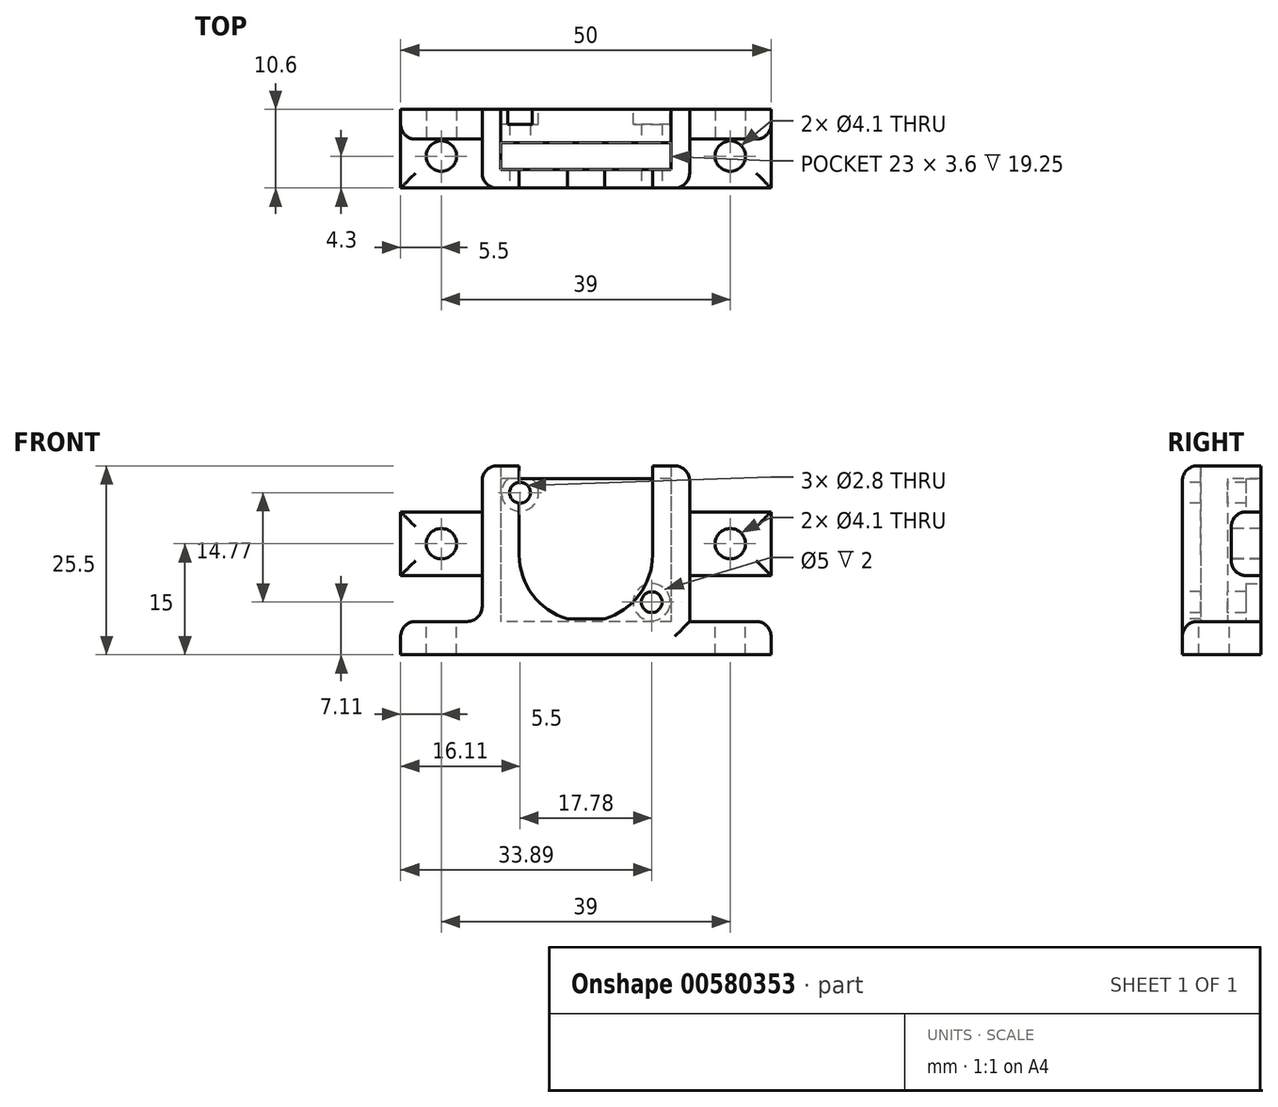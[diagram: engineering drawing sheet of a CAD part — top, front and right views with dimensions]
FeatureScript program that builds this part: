
annotation { "Feature Type Name" : "Feature", "Feature Type Description" : "" }
export const myFeature = defineFeature(function(context is Context, id is Id, definition is map)
    precondition{}
    {
        {
            var Q0;
            Q0=qCreatedBy(makeId("Top.planeOp"),FACE);
            var sketch = newSketch(context, id + "F0", { "sketchPlane" : qUnion([Q0])});
            skLineSegment(sketch, "E0.bottom", {"start": v(11.5, -1.8) * mm, "end": v(-11.5, -1.8) * mm});
            skLineSegment(sketch, "E0.top", {"start": v(11.5, 1.8) * mm, "end": v(-11.5, 1.8) * mm});
            skLineSegment(sketch, "E0.left", {"start": v(11.5, -1.8) * mm, "end": v(11.5, 1.8) * mm});
            skLineSegment(sketch, "E0.right", {"start": v(-11.5, -1.8) * mm, "end": v(-11.5, 1.8) * mm});
            skPoint(sketch, "E0.middle", {"position": v(0, 0) * mm});
            skLineSegment(sketch, "E1.bottom", {"start": v(14, -4.3) * mm, "end": v(-14, -4.3) * mm});
            skLineSegment(sketch, "E1.top", {"start": v(14, 4.3) * mm, "end": v(-14, 4.3) * mm});
            skLineSegment(sketch, "E1.left", {"start": v(14, -4.3) * mm, "end": v(14, 4.3) * mm});
            skLineSegment(sketch, "E1.right", {"start": v(-14, -4.3) * mm, "end": v(-14, 4.3) * mm});
            skSolve(sketch);
        }
        {
            var Q0;
            Q0 = qSketchRegion(id + "F0", true);
            extrude(context, id + "F1", {"entities" : qUnion([Q0]), "depth" : 21 * mm, "offsetDistance" : 25 * mm});
        }
        {
            var Q0;
            Q0=makeQuery(id+"F1.opExtrude","SWEPT_FACE",FACE,{"disambiguationData":[OSD([sQuery(id+"F0.wireOp",EDGE,"E1.bottom")])]});
            var sketch = newSketch(context, id + "F2", { "sketchPlane" : qUnion([Q0])});
            skPoint(sketch, "E2.start.orphan", {"position": v(-7.75, 9) * mm});
            skPoint(sketch, "E3.start.orphan", {"position": v(9.75, 9) * mm});
            skPoint(sketch, "E4.center.orphan", {"position": v(1, 9) * mm});
            skArc(sketch, "E5", {"start": v(-9, 9) * mm, "mid": v(-7.2, 3.6) * mm, "end": v(-2.5, 0.36) * mm});
            skLineSegment(sketch, "E6", {"start": v(9, 9) * mm, "end": v(9, 21) * mm});
            skLineSegment(sketch, "E7", {"start": v(-9, 9) * mm, "end": v(-9, 21) * mm});
            skPoint(sketch, "E8.orphan", {"position": v(-14, 9) * mm});
            skPoint(sketch, "E9.orphan", {"position": v(14, 9) * mm});
            skLineSegment(sketch, "E10", {"start": v(2.5, 0.36) * mm, "end": v(-2.5, 0.36) * mm});
            skArc(sketch, "E11.trimOffspring", {"start": v(2.5, 0.36) * mm, "mid": v(7.2, 3.6) * mm, "end": v(9, 9) * mm});
            skSolve(sketch);
        }
        {
            var Q0;
            Q0=makeQuery(id+"F2.imprint","IMPRINT",FACE,{"disambiguationData":[TD([[makeQuery(id+"F2.imprint","IMPRINT",EDGE,{"derivedFrom":sQuery(id+"F2.wireOp",EDGE,"E5")}),1.0]])]});
            extrude(context, id + "F3", {"entities" : qUnion([Q0]), "operationType" : NewBodyOperationType.REMOVE, "oppositeDirection" : true, "depth" : 2.5 * mm, "offsetDistance" : 25 * mm});
        }
        {
            var Q0;
            Q0=makeQuery(id+"F1.opExtrude","CAP_FACE",FACE,{"disambiguationData":[OSD([sQuery(id+"F0.wireOp",EDGE,"E0.bottom"),sQuery(id+"F0.wireOp",EDGE,"E0.top"),sQuery(id+"F0.wireOp",EDGE,"E0.left"),sQuery(id+"F0.wireOp",EDGE,"E0.right"),sQuery(id+"F0.wireOp",EDGE,"E1.bottom"),sQuery(id+"F0.wireOp",EDGE,"E1.top"),sQuery(id+"F0.wireOp",EDGE,"E1.left"),sQuery(id+"F0.wireOp",EDGE,"E1.right")])],"isStart":true});
            var sketch = newSketch(context, id + "F4", { "sketchPlane" : qUnion([Q0])});
            skLineSegment(sketch, "E12.bottom", {"start": v(-25, -4.3) * mm, "end": v(25, -4.3) * mm});
            skLineSegment(sketch, "E12.top", {"start": v(-25, 4.3) * mm, "end": v(25, 4.3) * mm});
            skLineSegment(sketch, "E12.left", {"start": v(-25, -4.3) * mm, "end": v(-25, 4.3) * mm});
            skLineSegment(sketch, "E12.right", {"start": v(25, -4.3) * mm, "end": v(25, 4.3) * mm});
            skPoint(sketch, "E12.middle", {"position": v(0, 0) * mm});
            skSolve(sketch);
        }
        {
            var Q0;
            Q0 = qSketchRegion(id + "F4", true);
            extrude(context, id + "F5", {"entities" : qUnion([Q0]), "operationType" : NewBodyOperationType.ADD, "depth" : 2.5 * mm, "offsetDistance" : 25 * mm});
        }
        {
            var Q0;
            {var subQ0=sQuery(id+"F4.wireOp",EDGE,"E12.top");var subQ1=sQuery(id+"F4.wireOp",EDGE,"E12.bottom");var subQ2=sQuery(id+"F4.wireOp",EDGE,"E12.left");Q0=makeQuery(id+"F5.boolean.opBoolean","SPLIT",FACE,{"disambiguationData":[TD([makeQuery(id+"F1.opExtrude","SWEPT_FACE",FACE,{"disambiguationData":[OSD([sQuery(id+"F0.wireOp",EDGE,"E1.right")])]})])],"derivedFrom":makeQuery(id+"F5.opExtrude","CAP_FACE",FACE,{"disambiguationData":[OSD([subQ1,subQ0,subQ2,sQuery(id+"F4.wireOp",EDGE,"E12.right")])],"isStart":true})});}
            var sketch = newSketch(context, id + "F6", { "sketchPlane" : qUnion([Q0])});
            skCircle(sketch, "E13", {"center": v(-19.5, 0) * mm, "radius": 2.05 * mm});
            skPoint(sketch, "E13.centerSnap0", {"position": v(-19.5, -2.3) * mm});
            skLineSegment(sketch, "E14", {"start": v(-19.5, -4.3) * mm, "end": v(-19.5, 4.3) * mm});
            skSolve(sketch);
        }
        {
            var Q0;
            Q0 = qSketchRegion(id + "F6", true);
            extrude(context, id + "F7", {"entities" : qUnion([Q0]), "operationType" : NewBodyOperationType.REMOVE, "oppositeDirection" : true, "depth" : 25 * mm, "offsetDistance" : 25 * mm});
        }
        {
            var Q0;
            {var subQ0=sQuery(id+"F4.wireOp",EDGE,"E12.bottom");var subQ1=sQuery(id+"F4.wireOp",EDGE,"E12.top");var subQ2=sQuery(id+"F4.wireOp",EDGE,"E12.right");Q0=makeQuery(id+"F5.boolean.opBoolean","SPLIT",FACE,{"disambiguationData":[TD([makeQuery(id+"F1.opExtrude","SWEPT_FACE",FACE,{"disambiguationData":[OSD([sQuery(id+"F0.wireOp",EDGE,"E1.left")])]})])],"derivedFrom":makeQuery(id+"F5.opExtrude","CAP_FACE",FACE,{"disambiguationData":[OSD([subQ0,subQ1,sQuery(id+"F4.wireOp",EDGE,"E12.left"),subQ2])],"isStart":true})});}
            var sketch = newSketch(context, id + "F8", { "sketchPlane" : qUnion([Q0])});
            skCircle(sketch, "E15", {"center": v(19.5, 0) * mm, "radius": 2.05 * mm});
            skPoint(sketch, "E15.centerSnap0", {"position": v(19.5, -2.05) * mm});
            skLineSegment(sketch, "E16", {"start": v(19.5, -4.3) * mm, "end": v(19.5, 4.3) * mm});
            skSolve(sketch);
        }
        {
            var Q0;
            Q0 = qSketchRegion(id + "F8", true);
            extrude(context, id + "F9", {"entities" : qUnion([Q0]), "operationType" : NewBodyOperationType.REMOVE, "oppositeDirection" : true, "depth" : 25 * mm, "offsetDistance" : 25 * mm});
        }
        {
            var Q0;
            Q0=makeQuery(id+"F1.opExtrude","CAP_FACE",FACE,{"disambiguationData":[OSD([sQuery(id+"F0.wireOp",EDGE,"E0.bottom"),sQuery(id+"F0.wireOp",EDGE,"E0.top"),sQuery(id+"F0.wireOp",EDGE,"E0.left"),sQuery(id+"F0.wireOp",EDGE,"E0.right"),sQuery(id+"F0.wireOp",EDGE,"E1.bottom"),sQuery(id+"F0.wireOp",EDGE,"E1.top"),sQuery(id+"F0.wireOp",EDGE,"E1.left"),sQuery(id+"F0.wireOp",EDGE,"E1.right")])],"isStart":false});
            var sketch = newSketch(context, id + "F10", { "sketchPlane" : qUnion([Q0])});
            skLineSegment(sketch, "E17.bottom", {"start": v(-11.5, -1.7) * mm, "end": v(11.5, -1.7) * mm});
            skLineSegment(sketch, "E17.top", {"start": v(-11.5, 1.7) * mm, "end": v(11.5, 1.7) * mm});
            skLineSegment(sketch, "E17.left", {"start": v(-11.5, -1.7) * mm, "end": v(-11.5, 1.7) * mm});
            skLineSegment(sketch, "E17.right", {"start": v(11.5, -1.7) * mm, "end": v(11.5, 1.7) * mm});
            skSolve(sketch);
        }
        {
            var Q0;
            Q0 = qSketchRegion(id + "F10", true);
            extrude(context, id + "F11", {"entities" : qUnion([Q0]), "operationType" : NewBodyOperationType.REMOVE, "oppositeDirection" : true, "depth" : 21 * mm, "offsetDistance" : 25 * mm});
        }
        {
            var Q0;
            Q0=makeQuery(id+"F1.opExtrude","SWEPT_FACE",FACE,{"disambiguationData":[OSD([sQuery(id+"F0.wireOp",EDGE,"E0.top")])]});
            var sketch = newSketch(context, id + "F12", { "sketchPlane" : qUnion([Q0])});
            skLineSegment(sketch, "E18.bottom", {"start": v(11.5, 17.25) * mm, "end": v(-11.5, 17.25) * mm});
            skLineSegment(sketch, "E18.top", {"start": v(11.5, 24.75) * mm, "end": v(-11.5, 24.75) * mm});
            skLineSegment(sketch, "E18.left", {"start": v(11.5, 17.25) * mm, "end": v(11.5, 24.75) * mm});
            skLineSegment(sketch, "E18.right", {"start": v(-11.5, 17.25) * mm, "end": v(-11.5, 24.75) * mm});
            skPoint(sketch, "E18.middle", {"position": v(0, 21) * mm});
            skSolve(sketch);
        }
        {
            var Q0;
            {var subQ0=sQuery(id+"F12.wireOp",EDGE,"E18.bottom");Q0=makeQuery(id+"F12.imprint","IMPRINT",FACE,{"disambiguationData":[TD([[makeQuery(id+"F12.imprint","IMPRINT",EDGE,{"derivedFrom":subQ0}),-1.0]])]});}
            extrude(context, id + "F13", {"entities" : qUnion([Q0]), "operationType" : NewBodyOperationType.REMOVE, "oppositeDirection" : true, "depth" : 25 * mm, "offsetDistance" : 25 * mm});
        }
        {
            var Q0;
            Q0=makeQuery(id+"F1.opExtrude","SWEPT_FACE",FACE,{"disambiguationData":[OSD([sQuery(id+"F0.wireOp",EDGE,"E1.left")])]});
            var sketch = newSketch(context, id + "F14", { "sketchPlane" : qUnion([Q0])});
            skLineSegment(sketch, "E19", {"start": v(4.3, 10.5) * mm, "end": v(4.3, 14.8) * mm});
            skLineSegment(sketch, "E20", {"start": v(4.3, 14.8) * mm, "end": v(4.3, 6.2) * mm});
            skLineSegment(sketch, "E21", {"start": v(4.3, 6.2) * mm, "end": v(2.3, 6.2) * mm});
            skLineSegment(sketch, "E22", {"start": v(2.3, 6.2) * mm, "end": v(2.3, 14.8) * mm});
            skLineSegment(sketch, "E23", {"start": v(2.3, 14.8) * mm, "end": v(4.3, 14.8) * mm});
            skSolve(sketch);
        }
        {
            var Q0;
            Q0 = qSketchRegion(id + "F14", true);
            extrude(context, id + "F15", {"entities" : qUnion([Q0]), "operationType" : NewBodyOperationType.ADD, "depth" : 11 * mm, "offsetDistance" : 25 * mm});
        }
        {
            var Q0;
            Q0=makeQuery(id+"F1.opExtrude","SWEPT_FACE",FACE,{"disambiguationData":[OSD([sQuery(id+"F0.wireOp",EDGE,"E1.right")])]});
            var sketch = newSketch(context, id + "F16", { "sketchPlane" : qUnion([Q0])});
            skLineSegment(sketch, "E24.bottom", {"start": v(-2.3, 14.8) * mm, "end": v(-6.3, 14.8) * mm});
            skLineSegment(sketch, "E24.top", {"start": v(-2.3, 6.2) * mm, "end": v(-6.3, 6.2) * mm});
            skLineSegment(sketch, "E24.left", {"start": v(-2.3, 14.8) * mm, "end": v(-2.3, 6.2) * mm});
            skPoint(sketch, "E24.middle", {"position": v(-4.3, 10.5) * mm});
            skLineSegment(sketch, "E25", {"start": v(-4.3, 6.2) * mm, "end": v(-4.3, 14.8) * mm});
            skSolve(sketch);
        }
        {
            var Q0;
            Q0 = qSketchRegion(id + "F16", true);
            extrude(context, id + "F17", {"entities" : qUnion([Q0]), "operationType" : NewBodyOperationType.ADD, "depth" : 11 * mm, "offsetDistance" : 25 * mm});
        }
        {
            var Q0;
            Q0=makeQuery(id+"F17.opExtrude","SWEPT_FACE",FACE,{"disambiguationData":[OSD([sQuery(id+"F16.wireOp",EDGE,"E24.left")])]});
            var sketch = newSketch(context, id + "F18", { "sketchPlane" : qUnion([Q0])});
            skLineSegment(sketch, "E26", {"start": v(-19.5, 6.2) * mm, "end": v(-19.5, 14.8) * mm});
            skCircle(sketch, "E27", {"center": v(-19.5, 10.5) * mm, "radius": 2.05 * mm});
            skSolve(sketch);
        }
        {
            var Q0;
            Q0=makeQuery(id+"F15.opExtrude","SWEPT_FACE",FACE,{"disambiguationData":[OSD([sQuery(id+"F14.wireOp",EDGE,"E22")])]});
            var sketch = newSketch(context, id + "F19", { "sketchPlane" : qUnion([Q0])});
            skLineSegment(sketch, "E28", {"start": v(19.5, 6.2) * mm, "end": v(19.5, 14.8) * mm});
            skCircle(sketch, "E29", {"center": v(19.5, 10.5) * mm, "radius": 2.05 * mm});
            skSolve(sketch);
        }
        {
            var Q0;
            {var subQ0=sQuery(id+"F18.wireOp",EDGE,"E27");var subQ1=sQuery(id+"F18.wireOp",EDGE,"E26");var subQ2=makeQuery(id+"F18.imprint","INTERSECT",VERTEX,{"disambiguationData":[OD(0.0)],"derivedFrom":[subQ1,subQ0]});Q0=makeQuery(id+"F18.imprint","IMPRINT",FACE,{"disambiguationData":[TD([[makeQuery(id+"F18.imprint","IMPRINT",EDGE,{"disambiguationData":[TD([[subQ2,-1.0]])],"derivedFrom":subQ1}),-1.0]])]});}
            var Q1;
            {var subQ0=sQuery(id+"F18.wireOp",EDGE,"E27");var subQ1=sQuery(id+"F18.wireOp",EDGE,"E26");var subQ2=makeQuery(id+"F18.imprint","INTERSECT",VERTEX,{"disambiguationData":[OD(0.0)],"derivedFrom":[subQ1,subQ0]});Q1=makeQuery(id+"F18.imprint","IMPRINT",FACE,{"disambiguationData":[TD([[makeQuery(id+"F18.imprint","IMPRINT",EDGE,{"disambiguationData":[TD([[subQ2,-1.0]])],"derivedFrom":subQ1}),1.0]])]});}
            var Q2;
            {var subQ0=sQuery(id+"F19.wireOp",EDGE,"E29");var subQ1=sQuery(id+"F19.wireOp",EDGE,"E28");var subQ2=makeQuery(id+"F19.imprint","INTERSECT",VERTEX,{"disambiguationData":[OD(0.0)],"derivedFrom":[subQ1,subQ0]});Q2=makeQuery(id+"F19.imprint","IMPRINT",FACE,{"disambiguationData":[TD([[makeQuery(id+"F19.imprint","IMPRINT",EDGE,{"disambiguationData":[TD([[subQ2,-1.0]])],"derivedFrom":subQ1}),1.0]])]});}
            var Q3;
            {var subQ0=sQuery(id+"F19.wireOp",EDGE,"E29");var subQ1=sQuery(id+"F19.wireOp",EDGE,"E28");var subQ2=makeQuery(id+"F19.imprint","INTERSECT",VERTEX,{"disambiguationData":[OD(0.0)],"derivedFrom":[subQ1,subQ0]});Q3=makeQuery(id+"F19.imprint","IMPRINT",FACE,{"disambiguationData":[TD([[makeQuery(id+"F19.imprint","IMPRINT",EDGE,{"disambiguationData":[TD([[subQ2,-1.0]])],"derivedFrom":subQ1}),-1.0]])]});}
            extrude(context, id + "F20", {"entities" : qUnion([Q0, Q1, Q2, Q3]), "operationType" : NewBodyOperationType.REMOVE, "oppositeDirection" : true, "depth" : 25 * mm, "offsetDistance" : 25 * mm});
        }
        {
            var Q0;
            Q0=makeQuery(id+"F5.opExtrude","CAP_EDGE",EDGE,{"disambiguationData":[OSD([sQuery(id+"F4.wireOp",EDGE,"E12.left")])],"isStart":true});
            var Q1;
            {var subQ0=sQuery(id+"F4.wireOp",EDGE,"E12.top");Q1=makeQuery(id+"F5.boolean.opBoolean","SPLIT",EDGE,{"disambiguationData":[TD([makeQuery(id+"F1.opExtrude","SWEPT_FACE",FACE,{"disambiguationData":[OSD([sQuery(id+"F0.wireOp",EDGE,"E1.right")])]})])],"derivedFrom":makeQuery(id+"F5.opExtrude","CAP_EDGE",EDGE,{"disambiguationData":[OSD([subQ0])],"isStart":true})});}
            var Q2;
            Q2=makeQuery(id+"F1.opExtrude","SWEPT_EDGE",EDGE,{"disambiguationData":[OSD([sQuery(id+"F0.wireOp",EDGE,"E1.bottom"),sQuery(id+"F0.wireOp",EDGE,"E1.right")])]});
            var Q3;
            Q3=makeQuery(id+"F1.opExtrude","CAP_EDGE",EDGE,{"disambiguationData":[OSD([sQuery(id+"F0.wireOp",EDGE,"E1.right")])],"isStart":true});
            var Q4;
            Q4=makeQuery(id+"F1.opExtrude","CAP_EDGE",EDGE,{"disambiguationData":[OSD([sQuery(id+"F0.wireOp",EDGE,"E1.right")])],"isStart":false});
            var Q5;
            {var subQ0=sQuery(id+"F0.wireOp",EDGE,"E1.right");var subQ1=sQuery(id+"F0.wireOp",EDGE,"E1.bottom");Q5=makeQuery(id+"F3.boolean.opBoolean","SPLIT",EDGE,{"disambiguationData":[TD([makeQuery(id+"F1.opExtrude","SWEPT_FACE",FACE,{"disambiguationData":[OSD([subQ0])]})])],"derivedFrom":makeQuery(id+"F1.opExtrude","CAP_EDGE",EDGE,{"disambiguationData":[OSD([subQ1])],"isStart":false})});}
            var Q6;
            {var subQ0=sQuery(id+"F4.wireOp",EDGE,"E12.top");Q6=makeQuery(id+"F5.boolean.opBoolean","SPLIT",EDGE,{"disambiguationData":[TD([makeQuery(id+"F1.opExtrude","SWEPT_FACE",FACE,{"disambiguationData":[OSD([sQuery(id+"F0.wireOp",EDGE,"E1.left")])]})])],"derivedFrom":makeQuery(id+"F5.opExtrude","CAP_EDGE",EDGE,{"disambiguationData":[OSD([subQ0])],"isStart":true})});}
            var Q7;
            Q7=makeQuery(id+"F1.opExtrude","SWEPT_EDGE",EDGE,{"disambiguationData":[OSD([sQuery(id+"F0.wireOp",EDGE,"E1.bottom"),sQuery(id+"F0.wireOp",EDGE,"E1.left")])]});
            var Q8;
            Q8=makeQuery(id+"F1.opExtrude","CAP_EDGE",EDGE,{"disambiguationData":[OSD([sQuery(id+"F0.wireOp",EDGE,"E1.left")])],"isStart":true});
            var Q9;
            Q9=makeQuery(id+"F1.opExtrude","CAP_EDGE",EDGE,{"disambiguationData":[OSD([sQuery(id+"F0.wireOp",EDGE,"E1.left")])],"isStart":false});
            var Q10;
            {var subQ0=sQuery(id+"F0.wireOp",EDGE,"E1.left");var subQ1=sQuery(id+"F0.wireOp",EDGE,"E1.bottom");Q10=makeQuery(id+"F3.boolean.opBoolean","SPLIT",EDGE,{"disambiguationData":[TD([makeQuery(id+"F1.opExtrude","SWEPT_FACE",FACE,{"disambiguationData":[OSD([subQ0])]})])],"derivedFrom":makeQuery(id+"F1.opExtrude","CAP_EDGE",EDGE,{"disambiguationData":[OSD([subQ1])],"isStart":false})});}
            var Q11;
            Q11=makeQuery(id+"F5.opExtrude","CAP_EDGE",EDGE,{"disambiguationData":[OSD([sQuery(id+"F4.wireOp",EDGE,"E12.right")])],"isStart":true});
            var Q12;
            Q12=makeQuery(id+"F15.opExtrude","CAP_EDGE",EDGE,{"disambiguationData":[OSD([sQuery(id+"F14.wireOp",EDGE,"E22")])],"isStart":true});
            var Q13;
            Q13=makeQuery(id+"F15.opExtrude","SWEPT_EDGE",EDGE,{"disambiguationData":[OSD([sQuery(id+"F14.wireOp",EDGE,"E22"),sQuery(id+"F14.wireOp",EDGE,"E23")])]});
            var Q14;
            Q14=makeQuery(id+"F15.opExtrude","SWEPT_EDGE",EDGE,{"disambiguationData":[OSD([sQuery(id+"F14.wireOp",EDGE,"E21"),sQuery(id+"F14.wireOp",EDGE,"E22")])]});
            var Q15;
            Q15=makeQuery(id+"F17.opExtrude","CAP_EDGE",EDGE,{"disambiguationData":[OSD([sQuery(id+"F16.wireOp",EDGE,"E24.bottom")])],"isStart":true});
            var Q16;
            Q16=makeQuery(id+"F17.opExtrude","CAP_EDGE",EDGE,{"disambiguationData":[OSD([sQuery(id+"F16.wireOp",EDGE,"E24.left")])],"isStart":true});
            var Q17;
            Q17=makeQuery(id+"F17.opExtrude","CAP_EDGE",EDGE,{"disambiguationData":[OSD([sQuery(id+"F16.wireOp",EDGE,"E24.top")])],"isStart":true});
            var Q18;
            Q18=makeQuery(id+"F17.opExtrude","SWEPT_EDGE",EDGE,{"disambiguationData":[OSD([sQuery(id+"F16.wireOp",EDGE,"E24.bottom"),sQuery(id+"F16.wireOp",EDGE,"E24.left")])]});
            var Q19;
            Q19=makeQuery(id+"F17.opExtrude","SWEPT_EDGE",EDGE,{"disambiguationData":[OSD([sQuery(id+"F16.wireOp",EDGE,"E24.top"),sQuery(id+"F16.wireOp",EDGE,"E24.left")])]});
            var Q20;
            Q20=makeQuery(id+"F17.opExtrude","CAP_EDGE",EDGE,{"disambiguationData":[OSD([sQuery(id+"F16.wireOp",EDGE,"E24.left")])],"isStart":false});
            var Q21;
            Q21=makeQuery(id+"F15.opExtrude","CAP_EDGE",EDGE,{"disambiguationData":[OSD([sQuery(id+"F14.wireOp",EDGE,"E22")])],"isStart":false});
            var Q22;
            Q22=makeQuery(id+"F3.boolean.opBoolean","COPY",EDGE,{"derivedFrom":makeQuery(id+"F3.opExtrude","CAP_EDGE",EDGE,{"disambiguationData":[OSD([sQuery(id+"F2.wireOp",EDGE,"E5")])],"isStart":true})});
            var Q23;
            Q23=makeQuery(id+"F3.boolean.opBoolean","COPY",EDGE,{"derivedFrom":makeQuery(id+"F3.opExtrude","CAP_EDGE",EDGE,{"disambiguationData":[OSD([sQuery(id+"F2.wireOp",EDGE,"E11.trimOffspring")])],"isStart":true})});
            var Q24;
            Q24=makeQuery(id+"F3.boolean.opBoolean","COPY",EDGE,{"derivedFrom":makeQuery(id+"F3.opExtrude","CAP_EDGE",EDGE,{"disambiguationData":[OSD([sQuery(id+"F2.wireOp",EDGE,"E10")])],"isStart":true})});
            fillet(context, id + "F21", {"entities" : qUnion([Q0, Q1, Q2, Q3, Q4, Q5, Q6, Q7, Q8, Q9, Q10, Q11, Q12, Q13, Q14, Q15, Q16, Q17, Q18, Q19, Q20, Q21, Q22, Q23, Q24]), "radius" : 2 * mm, "tangentPropagation" : true, "allowEdgeOverflow" : false});
        }
        {
            var Q0;
            Q0=makeQuery(id+"F1.opExtrude","SWEPT_FACE",FACE,{"disambiguationData":[OSD([sQuery(id+"F0.wireOp",EDGE,"E0.top")])]});
            var sketch = newSketch(context, id + "F22", { "sketchPlane" : qUnion([Q0])});
            skLineSegment(sketch, "E30.bottom", {"start": v(11.5, 0) * mm, "end": v(8.9, 0) * mm});
            skLineSegment(sketch, "E30.top", {"start": v(11.5, 2.6) * mm, "end": v(8.9, 2.6) * mm});
            skLineSegment(sketch, "E30.left", {"start": v(11.5, 0) * mm, "end": v(11.5, 2.61) * mm});
            skLineSegment(sketch, "E30.right", {"start": v(8.9, 0) * mm, "end": v(8.9, 2.6) * mm});
            skCircle(sketch, "E31", {"center": v(8.9, 2.6) * mm, "radius": 1.4 * mm});
            skLineSegment(sketch, "E32.bottom", {"start": v(-11.5, 0) * mm, "end": v(-8.9, 0) * mm});
            skLineSegment(sketch, "E32.top", {"start": v(-11.5, 17.38) * mm, "end": v(-8.9, 17.38) * mm});
            skLineSegment(sketch, "E32.left", {"start": v(-11.5, 0) * mm, "end": v(-11.5, 17.38) * mm});
            skLineSegment(sketch, "E32.right", {"start": v(-8.9, 0) * mm, "end": v(-8.9, 17.38) * mm});
            skCircle(sketch, "E33", {"center": v(-8.9, 17.38) * mm, "radius": 1.4 * mm});
            skSolve(sketch);
        }
        {
            var Q0;
            Q0=makeQuery(id+"F13.boolean.opBoolean","COPY",FACE,{"derivedFrom":makeQuery(id+"F13.opExtrude","SWEPT_FACE",FACE,{"disambiguationData":[OSD([sQuery(id+"F12.wireOp",EDGE,"E18.bottom")])]})});
            extrude(context, id + "F23", {"entities" : qUnion([Q0]), "operationType" : NewBodyOperationType.ADD, "depth" : 2 * mm, "offsetDistance" : 25 * mm});
        }
        {
            var Q0;
            {var subQ0=sQuery(id+"F4.wireOp",EDGE,"E12.bottom");var subQ1=sQuery(id+"F0.wireOp",EDGE,"E1.top");Q0=makeQuery(id+"F23.boolean.opBoolean","MERGE",FACE,{"derivedFrom":[makeQuery(id+"F17.boolean.opBoolean","MERGE",FACE,{"derivedFrom":[makeQuery(id+"F5.boolean.opBoolean","MERGE",FACE,{"derivedFrom":[makeQuery(id+"F1.opExtrude","SWEPT_FACE",FACE,{"disambiguationData":[OSD([subQ1])]}),makeQuery(id+"F5.opExtrude","SWEPT_FACE",FACE,{"disambiguationData":[OSD([subQ0])]})]}),makeQuery(id+"F17.opExtrude","SWEPT_FACE",FACE,{"disambiguationData":[OSD([sQuery(id+"F16.wireOp",EDGE,"E25")])]})]}),makeQuery(id+"F23.opExtrude","SWEPT_FACE",FACE,{"disambiguationData":[OSD([subQ1,subQ0,sQuery(id+"F12.wireOp",EDGE,"E18.bottom")])]})]});}
            var Q1;
            Q1=makeQuery(id+"F15.opExtrude","SWEPT_FACE",FACE,{"disambiguationData":[OSD([sQuery(id+"F14.wireOp",EDGE,"E20")])]});
            extrude(context, id + "F24", {"entities" : qUnion([Q0, Q1]), "operationType" : NewBodyOperationType.ADD, "depth" : 2 * mm, "offsetDistance" : 25 * mm});
        }
        {
            var Q0;
            {var subQ0=sQuery(id+"F22.wireOp",EDGE,"E30.right");var subQ1=sQuery(id+"F22.wireOp",EDGE,"E30.top");var subQ2=makeQuery(id+"F22.imprint","INTERSECT",VERTEX,{"derivedFrom":[subQ1,subQ0]});Q0=makeQuery(id+"F22.imprint","IMPRINT",FACE,{"disambiguationData":[TD([[makeQuery(id+"F22.imprint","IMPRINT",EDGE,{"disambiguationData":[TD([[subQ2,1.0]])],"derivedFrom":subQ1}),-1.0]])]});}
            var Q1;
            {var subQ0=sQuery(id+"F22.wireOp",EDGE,"E30.right");var subQ1=sQuery(id+"F22.wireOp",EDGE,"E30.top");var subQ2=makeQuery(id+"F22.imprint","INTERSECT",VERTEX,{"derivedFrom":[subQ1,subQ0]});Q1=makeQuery(id+"F22.imprint","IMPRINT",FACE,{"disambiguationData":[TD([[makeQuery(id+"F22.imprint","IMPRINT",EDGE,{"disambiguationData":[TD([[subQ2,1.0]])],"derivedFrom":subQ1}),1.0]])]});}
            var Q2;
            {var subQ0=sQuery(id+"F22.wireOp",EDGE,"E33");var subQ1=sQuery(id+"F22.wireOp",EDGE,"E32.right");var subQ2=makeQuery(id+"F22.imprint","INTERSECT",VERTEX,{"derivedFrom":[subQ1,subQ0]});Q2=makeQuery(id+"F22.imprint","IMPRINT",FACE,{"disambiguationData":[TD([[makeQuery(id+"F22.imprint","IMPRINT",EDGE,{"disambiguationData":[TD([[subQ2,-1.0]])],"derivedFrom":subQ1}),1.0]])]});}
            var Q3;
            {var subQ0=sQuery(id+"F22.wireOp",EDGE,"E32.right");var subQ1=sQuery(id+"F22.wireOp",EDGE,"E32.top");var subQ2=makeQuery(id+"F22.imprint","INTERSECT",VERTEX,{"derivedFrom":[subQ1,subQ0]});Q3=makeQuery(id+"F22.imprint","IMPRINT",FACE,{"disambiguationData":[TD([[makeQuery(id+"F22.imprint","IMPRINT",EDGE,{"disambiguationData":[TD([[subQ2,1.0]])],"derivedFrom":subQ1}),1.0]])]});}
            var Q4;
            {var subQ0=sQuery(id+"F22.wireOp",EDGE,"E33");var subQ1=sQuery(id+"F22.wireOp",EDGE,"E32.right");var subQ2=makeQuery(id+"F22.imprint","INTERSECT",VERTEX,{"derivedFrom":[subQ1,subQ0]});Q4=makeQuery(id+"F22.imprint","IMPRINT",FACE,{"disambiguationData":[TD([[makeQuery(id+"F22.imprint","IMPRINT",EDGE,{"disambiguationData":[TD([[subQ2,-1.0]])],"derivedFrom":subQ1}),-1.0]])]});}
            var Q5;
            {var subQ0=sQuery(id+"F22.wireOp",EDGE,"E32.right");var subQ1=sQuery(id+"F22.wireOp",EDGE,"E32.top");var subQ2=makeQuery(id+"F22.imprint","INTERSECT",VERTEX,{"derivedFrom":[subQ1,subQ0]});Q5=makeQuery(id+"F22.imprint","IMPRINT",FACE,{"disambiguationData":[TD([[makeQuery(id+"F22.imprint","IMPRINT",EDGE,{"disambiguationData":[TD([[subQ2,1.0]])],"derivedFrom":subQ1}),-1.0]])]});}
            extrude(context, id + "F25", {"entities" : qUnion([Q0, Q1, Q2, Q3, Q4, Q5]), "operationType" : NewBodyOperationType.REMOVE, "endBound" : BoundingType.SYMMETRIC, "oppositeDirection" : true, "depth" : 25 * mm, "offsetDistance" : 25 * mm});
        }
        {
            var Q0;
            Q0=makeQuery(id+"F24.opExtrude","CAP_FACE",FACE,{"disambiguationData":[OSD([sQuery(id+"F0.wireOp",EDGE,"E1.top"),sQuery(id+"F4.wireOp",EDGE,"E12.bottom"),sQuery(id+"F12.wireOp",EDGE,"E18.bottom"),sQuery(id+"F16.wireOp",EDGE,"E25")])],"isStart":false});
            var sketch = newSketch(context, id + "F26", { "sketchPlane" : qUnion([Q0])});
            skCircle(sketch, "E34", {"center": v(8.9, 17.38) * mm, "radius": 2.5 * mm});
            skCircle(sketch, "E35", {"center": v(-8.9, 2.6) * mm, "radius": 2.5 * mm});
            skSolve(sketch);
        }
        {
            var Q0;
            Q0 = qSketchRegion(id + "F26", true);
            extrude(context, id + "F27", {"entities" : qUnion([Q0]), "operationType" : NewBodyOperationType.REMOVE, "oppositeDirection" : true, "depth" : 2 * mm, "offsetDistance" : 25 * mm});
        }
        {
            var Q0;
            {var subQ0=sQuery(id+"F4.wireOp",EDGE,"E12.bottom");Q0=makeQuery(id+"F24.boolean.opBoolean","MERGE",FACE,{"derivedFrom":[makeQuery(id+"F5.opExtrude","CAP_FACE",FACE,{"disambiguationData":[OSD([subQ0,sQuery(id+"F4.wireOp",EDGE,"E12.top"),sQuery(id+"F4.wireOp",EDGE,"E12.left"),sQuery(id+"F4.wireOp",EDGE,"E12.right")])],"isStart":false}),makeQuery(id+"F24.opExtrude","SWEPT_FACE",FACE,{"disambiguationData":[OSD([subQ0]),TDD([makeQuery(id+"F5.opExtrude","CAP_EDGE",EDGE,{"disambiguationData":[OSD([subQ0])],"isStart":false})])]})]});}
            extrude(context, id + "F28", {"entities" : qUnion([Q0]), "operationType" : NewBodyOperationType.ADD, "depth" : 2 * mm, "offsetDistance" : 25 * mm});
        }
    });
